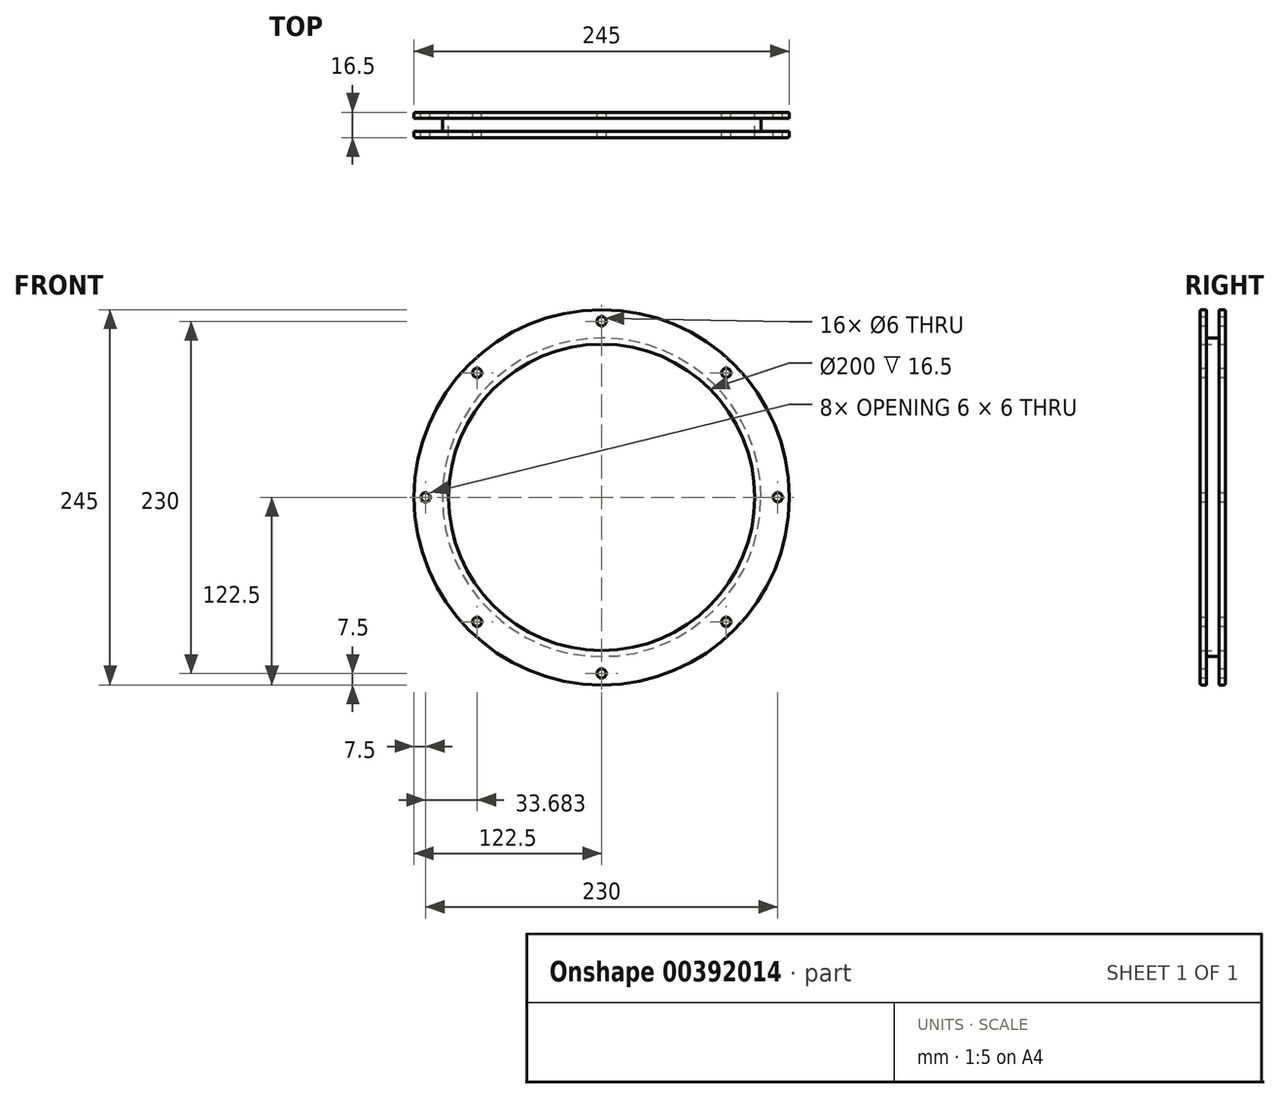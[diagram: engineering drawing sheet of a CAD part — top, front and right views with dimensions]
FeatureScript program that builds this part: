
annotation { "Feature Type Name" : "Feature", "Feature Type Description" : "" }
export const myFeature = defineFeature(function(context is Context, id is Id, definition is map)
    precondition{}
    {
        {
            var Q0;
            Q0=qCreatedBy(makeId("Front.planeOp"),FACE);
            var sketch = newSketch(context, id + "F0", { "sketchPlane" : qUnion([Q0])});
            skCircle(sketch, "E0", {"center": v(0, 0) * mm, "radius": 122.5 * mm});
            skArc(sketch, "E1", {"start": v(-7.37, 99.73) * mm, "mid": v(-70.71, 70.71) * mm, "end": v(-99.73, 7.37) * mm});
            skCircle(sketch, "E2", {"center": v(0, 0) * mm, "radius": 115 * mm, "construction": true});
            skCircle(sketch, "E3", {"center": v(-115, 0) * mm, "radius": 3 * mm});
            skPoint(sketch, "E4.orphan", {"position": v(-2, 105.37) * mm});
            skPoint(sketch, "E5.orphan", {"position": v(2, 105.37) * mm});
            skPoint(sketch, "E6.left.end.orphan", {"position": v(-105.96, -2) * mm});
            skPoint(sketch, "E6.left.start.orphan", {"position": v(-105.96, 2) * mm});
            skPoint(sketch, "E6.right.start.orphan", {"position": v(105.96, 2) * mm});
            skPoint(sketch, "E7.orphan", {"position": v(105.96, -2) * mm});
            skPoint(sketch, "E8.top.end.orphan", {"position": v(-2, -105.37) * mm});
            skPoint(sketch, "E8.top.start.orphan", {"position": v(2, -105.37) * mm});
            skPoint(sketch, "E9.visualSharp", {"position": v(-2, 99.98) * mm});
            skPoint(sketch, "E10.visualSharp", {"position": v(2, 99.98) * mm});
            skArc(sketch, "E11.trimOffspring", {"start": v(-99.73, -7.37) * mm, "mid": v(-70.71, -70.71) * mm, "end": v(-7.37, -99.73) * mm});
            skArc(sketch, "E12.trimOffspring", {"start": v(99.73, 7.37) * mm, "mid": v(70.71, 70.71) * mm, "end": v(7.37, 99.73) * mm});
            skArc(sketch, "E13.trimOffspring", {"start": v(7.37, -99.73) * mm, "mid": v(70.71, -70.71) * mm, "end": v(99.73, -7.37) * mm});
            skPoint(sketch, "E14.visualSharp", {"position": v(-99.98, 2) * mm});
            skPoint(sketch, "E15.visualSharp", {"position": v(-99.98, -2) * mm});
            skPoint(sketch, "E16.visualSharp", {"position": v(99.98, -2) * mm});
            skPoint(sketch, "E17.visualSharp", {"position": v(99.98, 2) * mm});
            skPoint(sketch, "E18.visualSharp", {"position": v(2, -99.98) * mm});
            skPoint(sketch, "E19.visualSharp", {"position": v(-2, -99.98) * mm});
            skCircle(sketch, "E20", {"center": v(0, 0) * mm, "radius": 100 * mm});
            skCircle(sketch, "E21.1.1", {"center": v(-81.32, -81.32) * mm, "radius": 3 * mm});
            skCircle(sketch, "E21.2.1", {"center": v(0, -115) * mm, "radius": 3 * mm});
            skCircle(sketch, "E21.3.1", {"center": v(81.32, -81.32) * mm, "radius": 3 * mm});
            skCircle(sketch, "E21.4.1", {"center": v(115, 0) * mm, "radius": 3 * mm});
            skCircle(sketch, "E21.5.1", {"center": v(81.32, 81.32) * mm, "radius": 3 * mm});
            skCircle(sketch, "E21.6.1", {"center": v(0, 115) * mm, "radius": 3 * mm});
            skCircle(sketch, "E21.7.1", {"center": v(-81.32, 81.32) * mm, "radius": 3 * mm});
            skSolve(sketch);
        }
        {
            var Q0;
            Q0=makeQuery(id+"F0.imprint","IMPRINT",FACE,{"disambiguationData":[TD([[makeQuery(id+"F0.imprint","IMPRINT",EDGE,{"derivedFrom":sQuery(id+"F0.wireOp",EDGE,"E0")}),1.0]])]});
            extrude(context, id + "F1", {"entities" : qUnion([Q0]), "depth" : 16.5 * mm});
        }
        {
            var Q0;
            Q0=qCreatedBy(makeId("Right.planeOp"),FACE);
            var sketch = newSketch(context, id + "F2", { "sketchPlane" : qUnion([Q0])});
            skLineSegment(sketch, "E22", {"start": v(0, 0) * mm, "end": v(0, 100) * mm});
            skLineSegment(sketch, "E23", {"start": v(0, 100) * mm, "end": v(0, 104) * mm});
            skLineSegment(sketch, "E24", {"start": v(0, 104) * mm, "end": v(-16.5, 104) * mm});
            skLineSegment(sketch, "E25", {"start": v(-16.5, 104) * mm, "end": v(-16.5, 100) * mm});
            skLineSegment(sketch, "E26", {"start": v(0, 104) * mm, "end": v(-4, 104) * mm});
            skLineSegment(sketch, "E27", {"start": v(-4, 104) * mm, "end": v(-4, 126.78) * mm});
            skLineSegment(sketch, "E28", {"start": v(-16.5, 104) * mm, "end": v(-12.5, 104) * mm});
            skLineSegment(sketch, "E29", {"start": v(-12.5, 104) * mm, "end": v(-12.5, 127.07) * mm});
            skLineSegment(sketch, "E30", {"start": v(-12.5, 127.07) * mm, "end": v(-4, 126.78) * mm});
            skLineSegment(sketch, "E31", {"start": v(0, 0) * mm, "end": v(60.08, 0) * mm, "construction": true});
            skSolve(sketch);
        }
        {
            var Q0;
            Q0=makeQuery(id+"F2.imprint","IMPRINT",FACE,{"disambiguationData":[TD([[makeQuery(id+"F2.imprint","IMPRINT",EDGE,{"derivedFrom":sQuery(id+"F2.wireOp",EDGE,"E24")}),-1.0]])]});
            var Q1;
            Q1=sQuery(id+"F2.wireOp",EDGE,"E31");
            revolve(context, id + "F3", {"operationType" : NewBodyOperationType.REMOVE, "entities" : qUnion([Q0]), "axis" : qUnion([Q1]), "revolveType" : RevolveType.FULL, "oppositeDirection" : true});
        }
        {
            var Q0;
            Q0=makeQuery(id+"F1.opExtrude","CAP_EDGE",EDGE,{"disambiguationData":[OSD([sQuery(id+"F0.wireOp",EDGE,"E0")])],"isStart":false});
            var Q1;
            Q1=makeQuery(id+"F1.opExtrude","CAP_EDGE",EDGE,{"disambiguationData":[OSD([sQuery(id+"F0.wireOp",EDGE,"E0")])],"isStart":true});
            fillet(context, id + "F4", {"entities" : qUnion([Q0, Q1]), "radius" : 1 * mm, "tangentPropagation" : true, "allowEdgeOverflow" : false});
        }
    });
